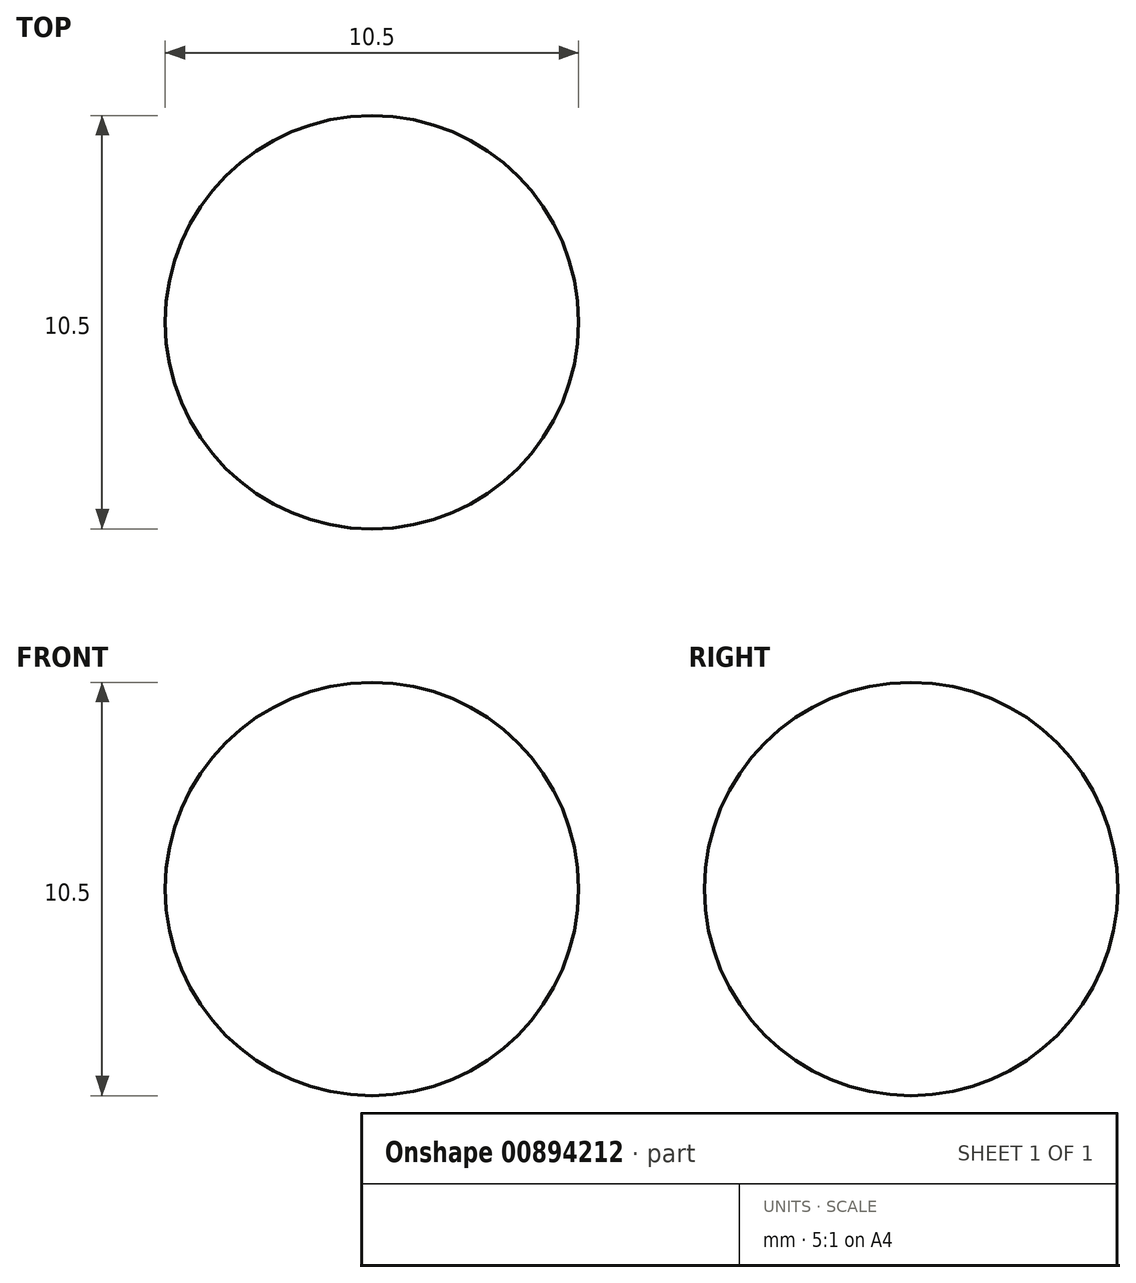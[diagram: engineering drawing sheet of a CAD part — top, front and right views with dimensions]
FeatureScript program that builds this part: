
annotation { "Feature Type Name" : "Feature", "Feature Type Description" : "" }
export const myFeature = defineFeature(function(context is Context, id is Id, definition is map)
    precondition{}
    {
        {
            var Q0;
            Q0=qCreatedBy(makeId("Front.planeOp"),FACE);
            var sketch = newSketch(context, id + "F0", { "sketchPlane" : qUnion([Q0])});
            skLineSegment(sketch, "E0", {"start": v(0, -5.25) * mm, "end": v(0, 5.25) * mm});
            skArc(sketch, "E1", {"start": v(0, -5.25) * mm, "mid": v(5.25, 0) * mm, "end": v(0, 5.25) * mm});
            skSolve(sketch);
        }
        {
            var Q0;
            Q0=makeQuery(id+"F0.imprint","IMPRINT",FACE,{"disambiguationData":[TD([[makeQuery(id+"F0.imprint","IMPRINT",EDGE,{"derivedFrom":sQuery(id+"F0.wireOp",EDGE,"E0")}),-1.0]])]});
            var Q1;
            Q1=sQuery(id+"F0.wireOp",EDGE,"E0");
            revolve(context, id + "F1", {"surfaceOperationType" : NewSurfaceOperationType.NEW, "entities" : qUnion([Q0]), "axis" : qUnion([Q1]), "revolveType" : RevolveType.FULL});
        }
    });
